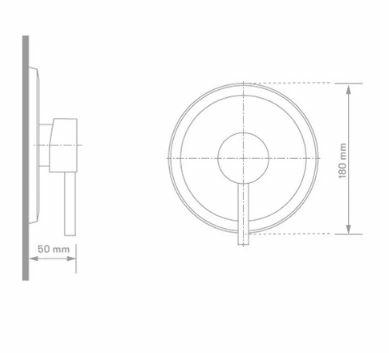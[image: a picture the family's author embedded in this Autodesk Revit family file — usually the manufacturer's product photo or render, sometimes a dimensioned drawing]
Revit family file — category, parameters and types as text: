
# Revit family: 01-3301-11SR-DUCHA KURVEN
name_source: partatom
category: Aparatos sanitarios
revit_build: Autodesk Revit 2018 (Build: 20170223_1515(x64)
units: mm (PartAtom-declared; Revit-internal decimal feet)

## family parameters
Anfitrión = Cara
Compartido = No
Corte con vacíos al cargar = No
Cota de conector redondo = Diámetro de uso
Número OmniClass = 23.31.11.00
Punto de cálculo de habitación = No
Tipo de pieza = Normal

## types (1)
- 01-3301-11SR
    Alto = 220 mm  [stored 0.721785 ft]
    Ancho = 130 mm
    Conexión AC = Sí
    Conexión AF = Sí
    Conexión de residuos = No
    Conexión de ventilación = No
    Descripción = DUCHA MONOMANDO
    Elevación por defecto = 0 mm  [stored 0 ft]
    Fabricante = Gricol
    Finish = <Por categoría>
    Imagen de tipo = <Ninguno>
    Largo = 120 mm
    Link Ficha Tecnica = https://infotecnica.gricol.com
    Modelo = 01-3301-11SR
    Product Name = DUCHA KURBEN
    URL = https://www.gricol.com

note: [stored X ft] marks values corroborated as IEEE doubles in the binary element streams (Revit-internal decimal feet)

## geometry (parser evidence)
native form markers: Blend x2, Sweep x3
no freeform markers — native parametric forms only
